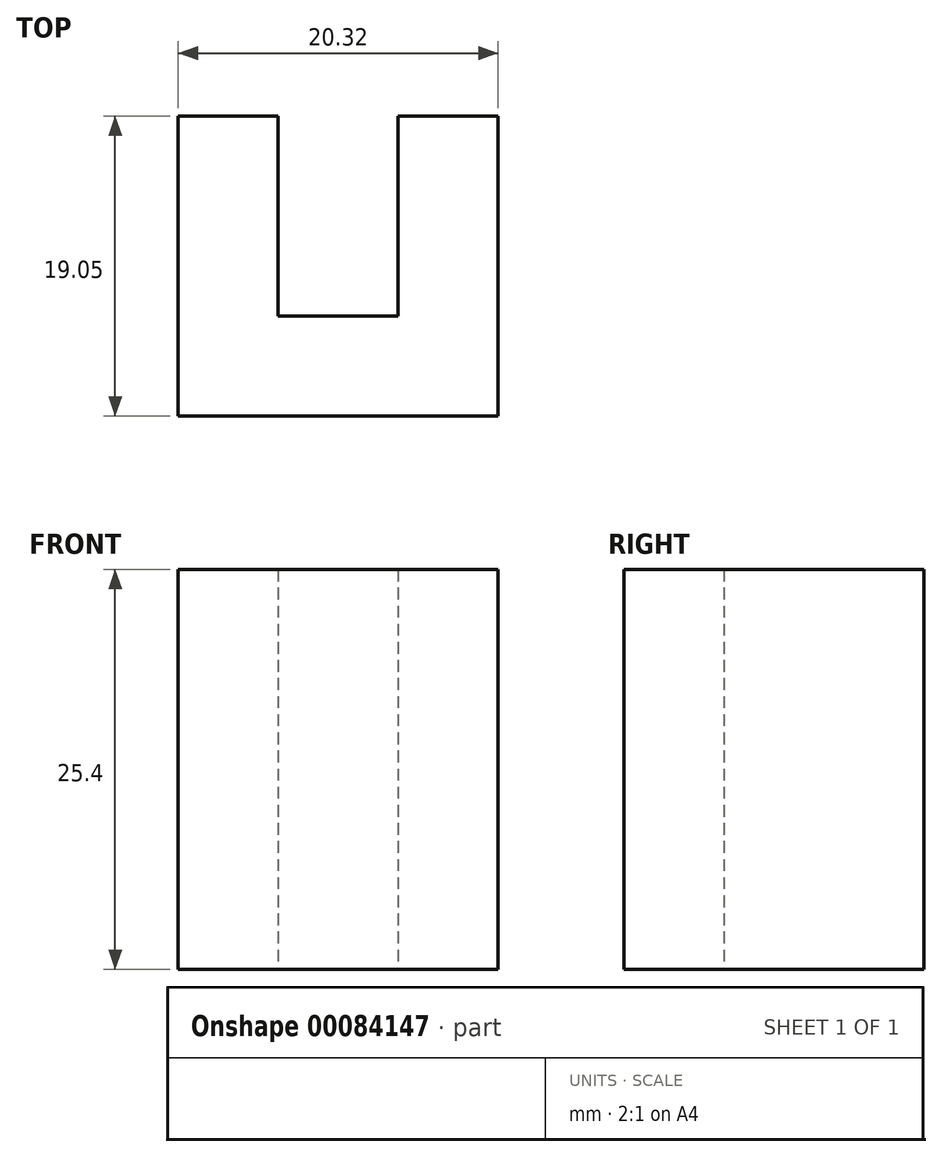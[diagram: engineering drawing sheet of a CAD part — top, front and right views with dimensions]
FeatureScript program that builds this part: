
annotation { "Feature Type Name" : "Feature", "Feature Type Description" : "" }
export const myFeature = defineFeature(function(context is Context, id is Id, definition is map)
    precondition{}
    {
        {
            var Q0;
            Q0=qCreatedBy(makeId("Top.planeOp"),FACE);
            var sketch = newSketch(context, id + "F0", { "sketchPlane" : qUnion([Q0])});
            skLineSegment(sketch, "E0.top", {"start": v(-2.72, -12.7) * mm, "end": v(4.9, -12.7) * mm});
            skLineSegment(sketch, "E0.left", {"start": v(-2.72, 0) * mm, "end": v(-2.72, -12.7) * mm});
            skLineSegment(sketch, "E0.right", {"start": v(4.9, 0) * mm, "end": v(4.9, -12.7) * mm});
            skLineSegment(sketch, "E1.0", {"start": v(11.25, 0) * mm, "end": v(11.25, -19.05) * mm});
            skLineSegment(sketch, "E1.1", {"start": v(-9.07, -19.05) * mm, "end": v(11.25, -19.05) * mm});
            skLineSegment(sketch, "E1.2", {"start": v(-9.07, 0) * mm, "end": v(-9.07, -19.05) * mm});
            skLineSegment(sketch, "E2", {"start": v(-9.07, 0) * mm, "end": v(-2.72, 0) * mm});
            skLineSegment(sketch, "E3.trimOffspring", {"start": v(4.9, 0) * mm, "end": v(11.25, 0) * mm});
            skSolve(sketch);
        }
        {
            var Q0;
            Q0 = qSketchRegion(id + "F0", true);
            extrude(context, id + "F1", {"entities" : qUnion([Q0]), "depth" : 25.4 * mm});
        }
    });
